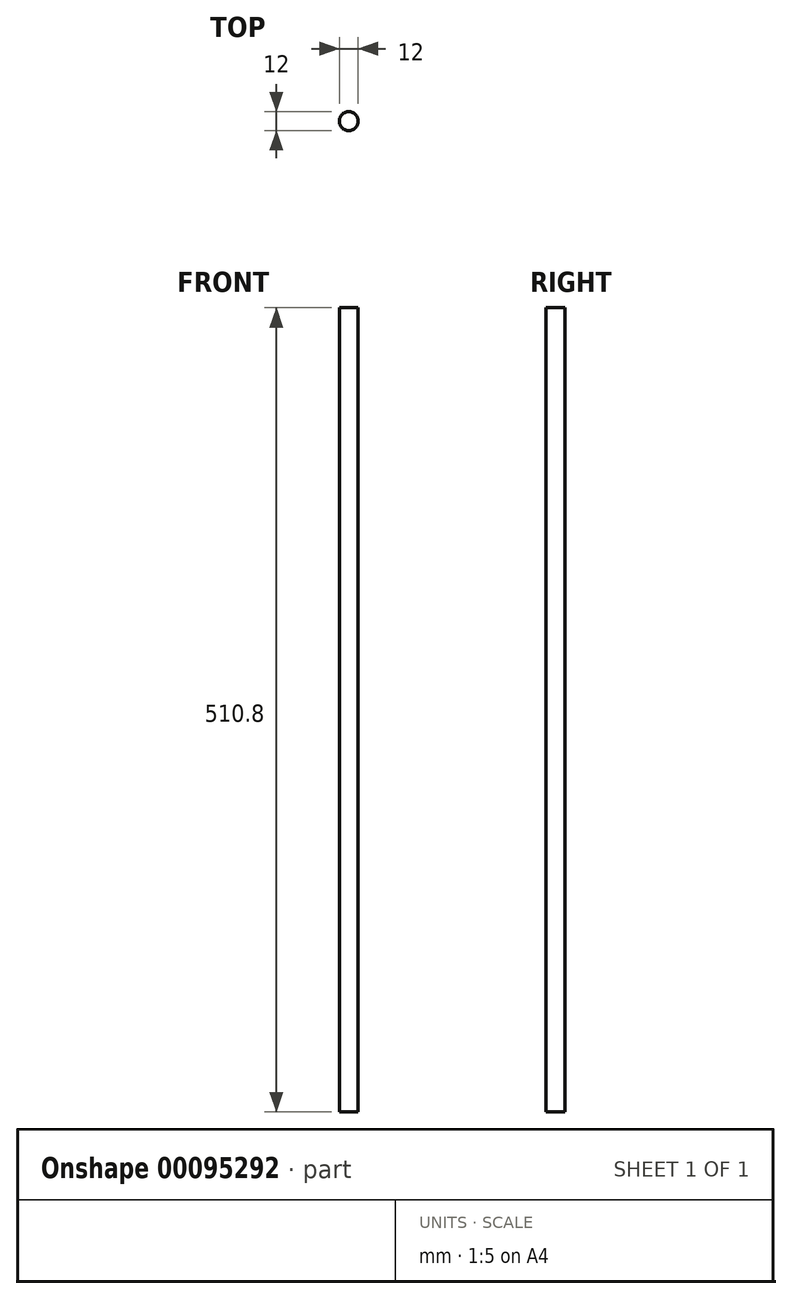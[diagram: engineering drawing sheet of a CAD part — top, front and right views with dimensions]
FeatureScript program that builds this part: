
annotation { "Feature Type Name" : "Feature", "Feature Type Description" : "" }
export const myFeature = defineFeature(function(context is Context, id is Id, definition is map)
    precondition{}
    {
        {
            var Q0;
            Q0=qCreatedBy(makeId("Top.planeOp"),FACE);
            var sketch = newSketch(context, id + "F0", { "sketchPlane" : qUnion([Q0])});
            skCircle(sketch, "E0", {"center": v(0, 0) * mm, "radius": 6 * mm});
            skSolve(sketch);
        }
        {
            var Q0;
            Q0 = qSketchRegion(id + "F0", true);
            extrude(context, id + "F1", {"entities" : qUnion([Q0]), "depth" : 510.8 * mm});
        }
    });
